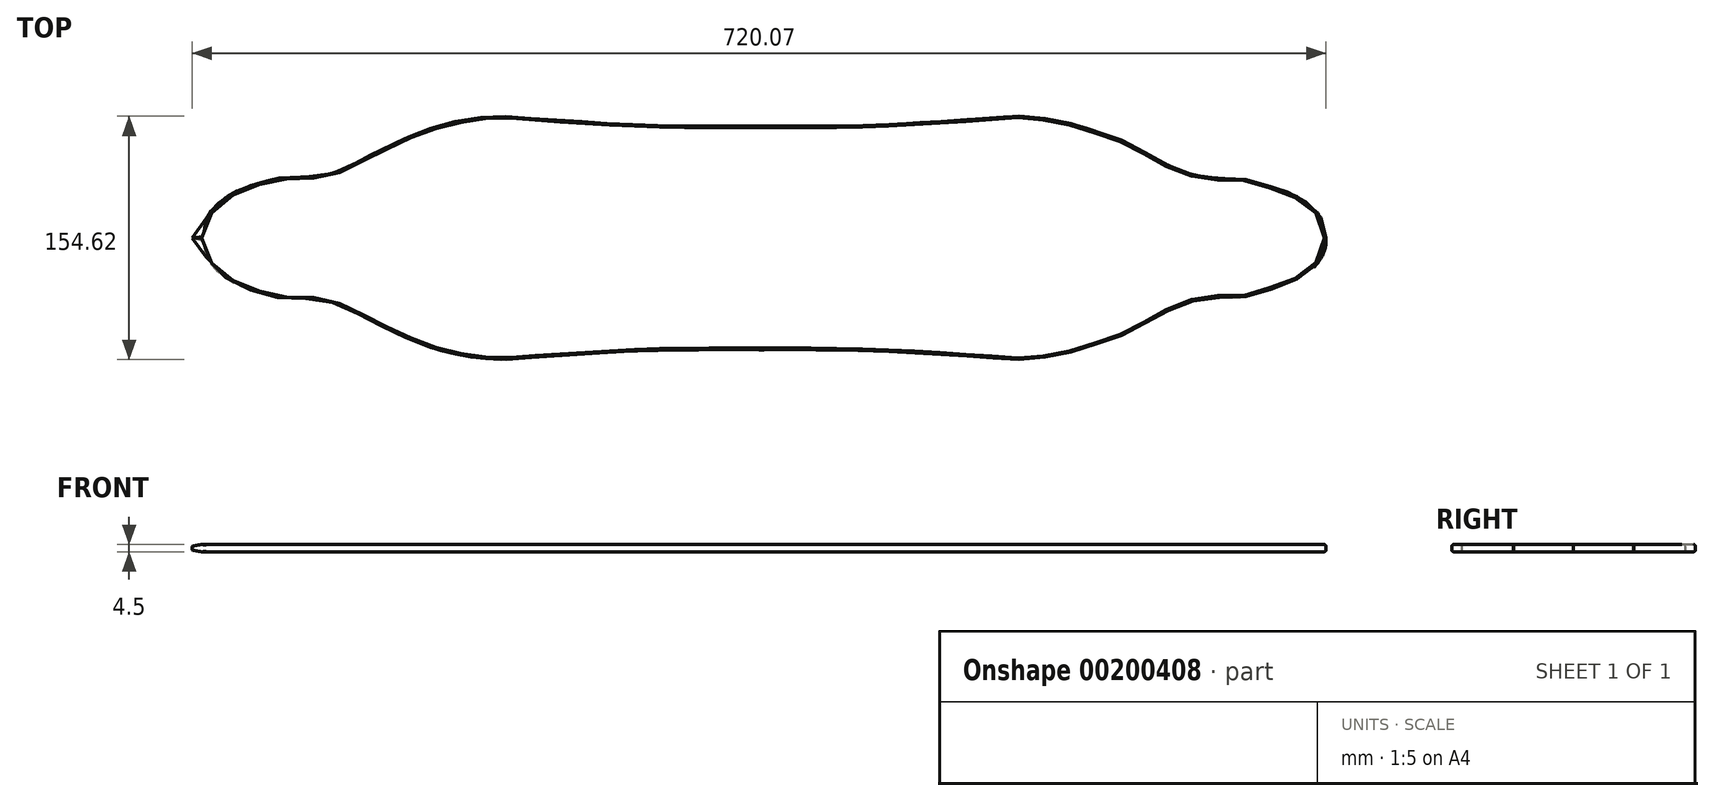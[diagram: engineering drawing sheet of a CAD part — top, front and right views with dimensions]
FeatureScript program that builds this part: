
annotation { "Feature Type Name" : "Feature", "Feature Type Description" : "" }
export const myFeature = defineFeature(function(context is Context, id is Id, definition is map)
    precondition{}
    {
        {
            var Q0;
            Q0=qCreatedBy(makeId("Top.planeOp"),FACE);
            var sketch = newSketch(context, id + "F0", { "sketchPlane" : qUnion([Q0])});
            skFitSpline(sketch, "E0", {"points": [v(0, 71.04) * mm, v(36.96, 71.04) * mm, v(74.57, 71.74) * mm, v(118.8, 74.17) * mm, v(153.62, 76.61) * mm, v(164.06, 77.3) * mm, v(174.5, 76.61) * mm, v(195.1, 73.33) * mm, v(213.72, 67.66) * mm, v(232.04, 61.19) * mm, v(249.85, 51.47) * mm, v(265.54, 43.37) * mm, v(276.57, 39.73) * mm, v(291.15, 37.7) * mm, v(304, 38.1) * mm, v(314.53, 35.68) * mm, v(323.84, 32.85) * mm, v(334.41, 29.6) * mm, v(348.23, 22.22) * mm, v(354.3, 16.55) * mm, v(359.49, 7.31) * mm, v(360, 0) * mm], "startDerivative": vector(527.59, -1.24) * mm, "endDerivative": vector(-7.74, -231.73) * mm});
            skFitSpline(sketch, "E1.MirrorCS", {"points": [v(0, 71.04) * mm, v(-36.96, 71.04) * mm, v(-74.57, 71.74) * mm, v(-118.8, 74.17) * mm, v(-153.62, 76.61) * mm, v(-164.06, 77.3) * mm, v(-174.5, 76.61) * mm, v(-195.1, 73.33) * mm, v(-213.72, 67.66) * mm, v(-231.93, 59.57) * mm, v(-249.34, 51.06) * mm, v(-261.09, 45) * mm, v(-274.45, 40.13) * mm, v(-291.45, 38.51) * mm, v(-304, 38.1) * mm, v(-314.53, 35.68) * mm, v(-323.84, 32.85) * mm, v(-338.41, 25.56) * mm, v(-349.75, 14.63) * mm, v(-352.18, 6.53) * mm, v(-360, 0) * mm], "startDerivative": vector(-527.59, -1.24) * mm, "endDerivative": vector(-674, 0) * mm});
            skFitSpline(sketch, "E2.MirrorCS", {"points": [v(0, -71.04) * mm, v(36.96, -71.04) * mm, v(74.57, -71.74) * mm, v(118.8, -74.17) * mm, v(153.62, -76.61) * mm, v(164.06, -77.3) * mm, v(174.5, -76.61) * mm, v(195.1, -73.33) * mm, v(213.72, -67.66) * mm, v(232.04, -61.19) * mm, v(249.85, -51.47) * mm, v(265.54, -43.37) * mm, v(276.57, -39.73) * mm, v(291.15, -37.7) * mm, v(304, -38.1) * mm, v(314.53, -35.68) * mm, v(323.84, -32.85) * mm, v(334.41, -29.6) * mm, v(348.23, -22.22) * mm, v(354.3, -16.55) * mm, v(359.49, -7.31) * mm, v(360, 0) * mm], "startDerivative": vector(527.59, 1.24) * mm, "endDerivative": vector(-7.74, 231.73) * mm});
            skLineSegment(sketch, "E3", {"start": v(360, 0) * mm, "end": v(-360, 0) * mm, "construction": true});
            skLineSegment(sketch, "E4", {"start": v(0, 71.04) * mm, "end": v(0, -71.04) * mm, "construction": true});
            skFitSpline(sketch, "E5.MirrorCS", {"points": [v(0, -71.04) * mm, v(-36.96, -71.04) * mm, v(-74.57, -71.74) * mm, v(-118.8, -74.17) * mm, v(-153.62, -76.61) * mm, v(-164.06, -77.3) * mm, v(-174.5, -76.61) * mm, v(-195.1, -73.33) * mm, v(-213.72, -67.66) * mm, v(-231.93, -59.57) * mm, v(-249.34, -51.06) * mm, v(-261.09, -45) * mm, v(-274.45, -40.13) * mm, v(-291.45, -38.51) * mm, v(-304, -38.1) * mm, v(-314.53, -35.68) * mm, v(-323.84, -32.85) * mm, v(-338.41, -25.56) * mm, v(-349.75, -14.63) * mm, v(-352.18, -6.53) * mm, v(-360, 0) * mm], "startDerivative": vector(-527.59, 1.24) * mm, "endDerivative": vector(-674, 0) * mm});
            skSolve(sketch);
        }
        {
            var Q0;
            Q0=makeQuery(id+"F0.imprint","IMPRINT",FACE,{"disambiguationData":[TD([[makeQuery(id+"F0.imprint","IMPRINT",EDGE,{"derivedFrom":sQuery(id+"F0.wireOp",EDGE,"E0")}),-1.0]])]});
            extrude(context, id + "F1", {"entities" : qUnion([Q0]), "depth" : 4.5 * mm});
        }
        {
            var Q0;
            Q0=makeQuery(id+"F1.opExtrude","CAP_EDGE",EDGE,{"disambiguationData":[OSD([sQuery(id+"F0.wireOp",EDGE,"E1.MirrorCS")])],"isStart":false});
            var Q1;
            Q1=makeQuery(id+"F1.opExtrude","CAP_EDGE",EDGE,{"disambiguationData":[OSD([sQuery(id+"F0.wireOp",EDGE,"E0")])],"isStart":false});
            var Q2;
            Q2=makeQuery(id+"F1.opExtrude","CAP_EDGE",EDGE,{"disambiguationData":[OSD([sQuery(id+"F0.wireOp",EDGE,"E0")])],"isStart":true});
            var Q3;
            Q3=makeQuery(id+"F1.opExtrude","CAP_EDGE",EDGE,{"disambiguationData":[OSD([sQuery(id+"F0.wireOp",EDGE,"E1.MirrorCS")])],"isStart":true});
            var Q4;
            Q4=makeQuery(id+"F1.opExtrude","CAP_EDGE",EDGE,{"disambiguationData":[OSD([sQuery(id+"F0.wireOp",EDGE,"E2.MirrorCS")])],"isStart":false});
            var Q5;
            Q5=makeQuery(id+"F1.opExtrude","CAP_EDGE",EDGE,{"disambiguationData":[OSD([sQuery(id+"F0.wireOp",EDGE,"E5.MirrorCS")])],"isStart":false});
            var Q6;
            Q6=makeQuery(id+"F1.opExtrude","CAP_EDGE",EDGE,{"disambiguationData":[OSD([sQuery(id+"F0.wireOp",EDGE,"E5.MirrorCS")])],"isStart":true});
            var Q7;
            Q7=makeQuery(id+"F1.opExtrude","CAP_EDGE",EDGE,{"disambiguationData":[OSD([sQuery(id+"F0.wireOp",EDGE,"E2.MirrorCS")])],"isStart":true});
            fillet(context, id + "F2", {"entities" : qUnion([Q0, Q1, Q2, Q3, Q4, Q5, Q6, Q7]), "radius" : 1 * mm, "tangentPropagation" : true, "allowEdgeOverflow" : false});
        }
    });
